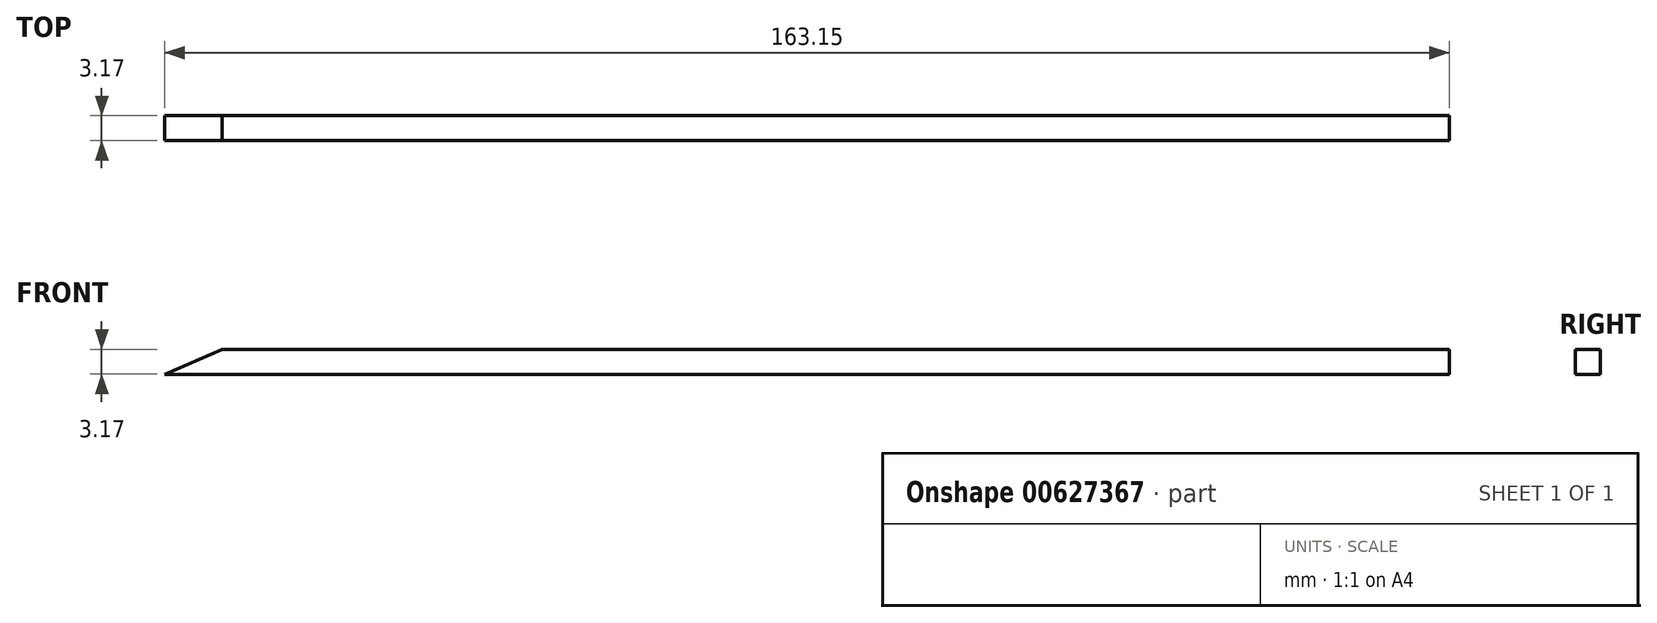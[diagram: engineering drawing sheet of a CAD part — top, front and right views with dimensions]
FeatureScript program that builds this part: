
annotation { "Feature Type Name" : "Feature", "Feature Type Description" : "" }
export const myFeature = defineFeature(function(context is Context, id is Id, definition is map)
    precondition{}
    {
        {
            var Q0;
            Q0=qCreatedBy(makeId("Front.planeOp"),FACE);
            var sketch = newSketch(context, id + "F0", { "sketchPlane" : qUnion([Q0])});
            skLineSegment(sketch, "E0", {"start": v(-106.66, 11.55) * mm, "end": v(49.22, 11.55) * mm});
            skLineSegment(sketch, "E1", {"start": v(49.22, 11.55) * mm, "end": v(49.22, 8.38) * mm});
            skLineSegment(sketch, "E2", {"start": v(49.22, 8.38) * mm, "end": v(-113.93, 8.38) * mm});
            skLineSegment(sketch, "E3", {"start": v(-113.93, 8.38) * mm, "end": v(-106.66, 11.55) * mm});
            skSolve(sketch);
        }
        {
            var Q0;
            Q0=makeQuery(id+"F0.imprint","IMPRINT",FACE,{"disambiguationData":[TD([[makeQuery(id+"F0.imprint","IMPRINT",EDGE,{"derivedFrom":sQuery(id+"F0.wireOp",EDGE,"E0")}),-1.0]])]});
            extrude(context, id + "F1", {"entities" : qUnion([Q0]), "depth" : 3.17 * mm, "offsetDistance" : 25.4 * mm});
        }
    });
